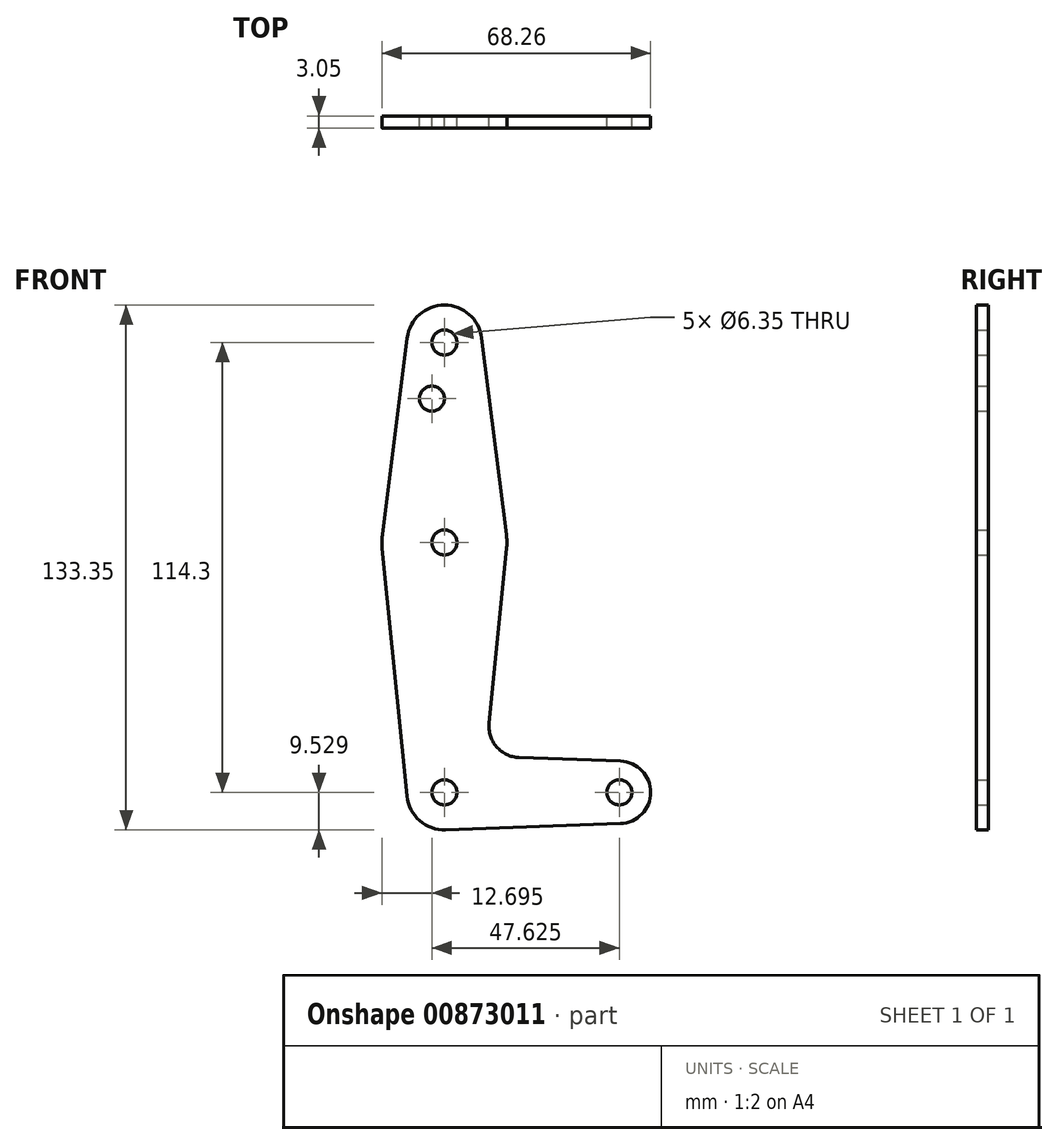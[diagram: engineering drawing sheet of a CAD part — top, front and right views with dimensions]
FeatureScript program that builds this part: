
annotation { "Feature Type Name" : "Feature", "Feature Type Description" : "" }
export const myFeature = defineFeature(function(context is Context, id is Id, definition is map)
    precondition{}
    {
        {
            var Q0;
            Q0=qCreatedBy(makeId("Front.planeOp"),FACE);
            var sketch = newSketch(context, id + "F0", { "sketchPlane" : qUnion([Q0])});
            skLineSegment(sketch, "E0", {"start": v(-41.12, 53.89) * mm, "end": v(-41.12, -60.41) * mm, "construction": true});
            skLineSegment(sketch, "E1", {"start": v(-41.12, -60.41) * mm, "end": v(3.33, -60.41) * mm, "construction": true});
            skCircle(sketch, "E2", {"center": v(-41.12, 53.89) * mm, "radius": 9.53 * mm});
            skCircle(sketch, "E3", {"center": v(-41.12, -60.41) * mm, "radius": 9.53 * mm});
            skCircle(sketch, "E4", {"center": v(3.33, -60.41) * mm, "radius": 7.94 * mm});
            skCircle(sketch, "E5", {"center": v(-41.12, 3.09) * mm, "radius": 15.88 * mm});
            skLineSegment(sketch, "E6", {"start": v(-50.57, 55.08) * mm, "end": v(-56.87, 5.07) * mm});
            skLineSegment(sketch, "E7", {"start": v(-56.92, 1.5) * mm, "end": v(-50.6, -61.36) * mm});
            skLineSegment(sketch, "E8", {"start": v(-31.67, 55.08) * mm, "end": v(-25.37, 5.07) * mm});
            skLineSegment(sketch, "E9", {"start": v(-40.78, -69.93) * mm, "end": v(3.61, -68.34) * mm});
            skCircle(sketch, "E10", {"center": v(-41.12, 53.89) * mm, "radius": 3.18 * mm});
            skCircle(sketch, "E11", {"center": v(-41.12, 3.09) * mm, "radius": 3.18 * mm});
            skCircle(sketch, "E12", {"center": v(-41.12, -60.41) * mm, "radius": 3.18 * mm});
            skCircle(sketch, "E13", {"center": v(3.33, -60.41) * mm, "radius": 3.18 * mm});
            skCircle(sketch, "E14", {"center": v(-44.3, 39.61) * mm, "radius": 3.18 * mm});
            skLineSegment(sketch, "E15", {"start": v(-25.32, 1.5) * mm, "end": v(-29.78, -42.82) * mm});
            skLineSegment(sketch, "E16", {"start": v(-22.15, -51.56) * mm, "end": v(3.61, -52.48) * mm});
            skArc(sketch, "E17.filletArc", {"start": v(-29.78, -42.82) * mm, "mid": v(-27.86, -48.84) * mm, "end": v(-22.15, -51.56) * mm});
            skSolve(sketch);
        }
        {
            var Q0;
            Q0 = qSketchRegion(id + "F0", true);
            extrude(context, id + "F1", {"entities" : qUnion([Q0]), "depth" : 3.05 * mm, "offsetDistance" : 25.4 * mm});
        }
    });
